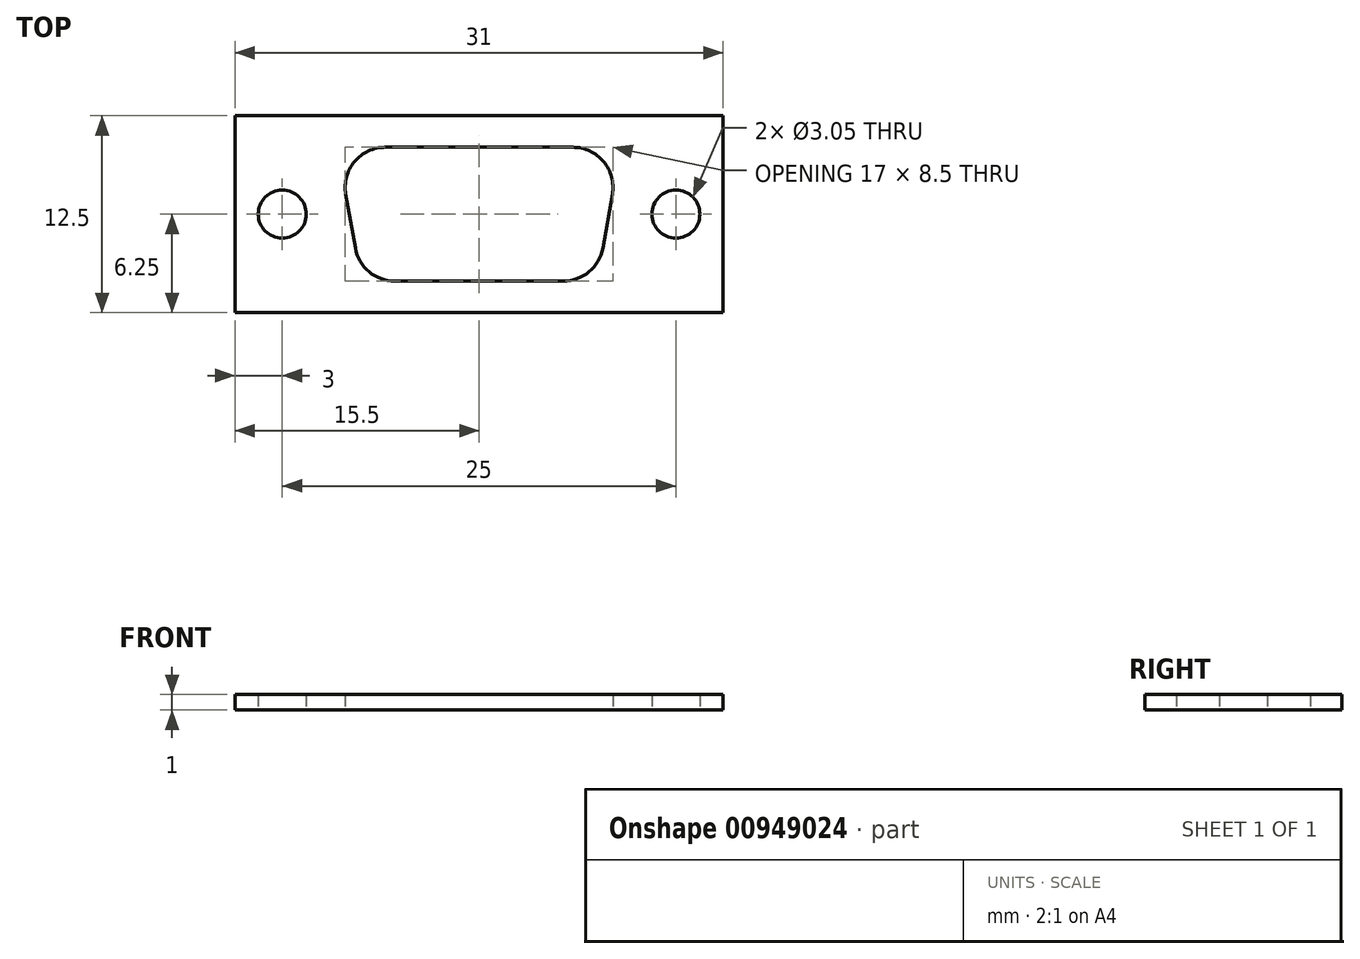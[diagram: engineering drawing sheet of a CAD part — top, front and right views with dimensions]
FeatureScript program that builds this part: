
annotation { "Feature Type Name" : "Feature", "Feature Type Description" : "" }
export const myFeature = defineFeature(function(context is Context, id is Id, definition is map)
    precondition{}
    {
        {
            var Q0;
            Q0=qCreatedBy(makeId("Top.planeOp"),FACE);
            var sketch = newSketch(context, id + "F0", { "sketchPlane" : qUnion([Q0])});
            skLineSegment(sketch, "E0", {"start": v(-24.66, 0) * mm, "end": v(28.2, 0) * mm, "construction": true});
            skLineSegment(sketch, "E1", {"start": v(0, 19.67) * mm, "end": v(0, -26.12) * mm, "construction": true});
            skLineSegment(sketch, "E2.bottom", {"start": v(-15.5, 6.25) * mm, "end": v(15.5, 6.25) * mm});
            skLineSegment(sketch, "E2.top", {"start": v(-15.5, -6.25) * mm, "end": v(15.5, -6.25) * mm});
            skLineSegment(sketch, "E2.left", {"start": v(-15.5, 6.25) * mm, "end": v(-15.5, -6.25) * mm});
            skLineSegment(sketch, "E2.right", {"start": v(15.5, 6.25) * mm, "end": v(15.5, -6.25) * mm});
            skPoint(sketch, "E2.middle", {"position": v(0, 0) * mm});
            skCircle(sketch, "E3", {"center": v(-12.5, 0) * mm, "radius": 1.52 * mm});
            skCircle(sketch, "E4", {"center": v(12.5, 0) * mm, "radius": 1.52 * mm});
            skLineSegment(sketch, "E5", {"start": v(-5.96, 4.25) * mm, "end": v(0, 4.25) * mm});
            skLineSegment(sketch, "E6", {"start": v(-5.36, -4.25) * mm, "end": v(0, -4.25) * mm});
            skLineSegment(sketch, "E7", {"start": v(-7.86, -2.15) * mm, "end": v(-8.46, 1.27) * mm});
            skArc(sketch, "E8", {"start": v(-5.96, 4.25) * mm, "mid": v(-7.9, 3.34) * mm, "end": v(-8.46, 1.27) * mm});
            skArc(sketch, "E9", {"start": v(-7.86, -2.15) * mm, "mid": v(-6.99, -3.66) * mm, "end": v(-5.36, -4.25) * mm});
            skLineSegment(sketch, "E10.MirrorCS", {"start": v(5.96, 4.25) * mm, "end": v(0, 4.25) * mm});
            skArc(sketch, "E11.MirrorCS", {"start": v(5.96, 4.25) * mm, "mid": v(7.9, 3.34) * mm, "end": v(8.46, 1.27) * mm});
            skLineSegment(sketch, "E12.MirrorCS", {"start": v(7.86, -2.15) * mm, "end": v(8.46, 1.27) * mm});
            skArc(sketch, "E13.MirrorCS", {"start": v(7.86, -2.15) * mm, "mid": v(6.99, -3.66) * mm, "end": v(5.36, -4.25) * mm});
            skLineSegment(sketch, "E14.MirrorCS", {"start": v(5.36, -4.25) * mm, "end": v(0, -4.25) * mm});
            skSolve(sketch);
        }
        {
            var Q0;
            Q0=makeQuery(id+"F0.imprint","IMPRINT",FACE,{"disambiguationData":[TD([[makeQuery(id+"F0.imprint","IMPRINT",EDGE,{"derivedFrom":sQuery(id+"F0.wireOp",EDGE,"E2.bottom")}),-1.0]])]});
            extrude(context, id + "F1", {"entities" : qUnion([Q0]), "depth" : 1 * mm, "offsetDistance" : 25 * mm});
        }
    });
